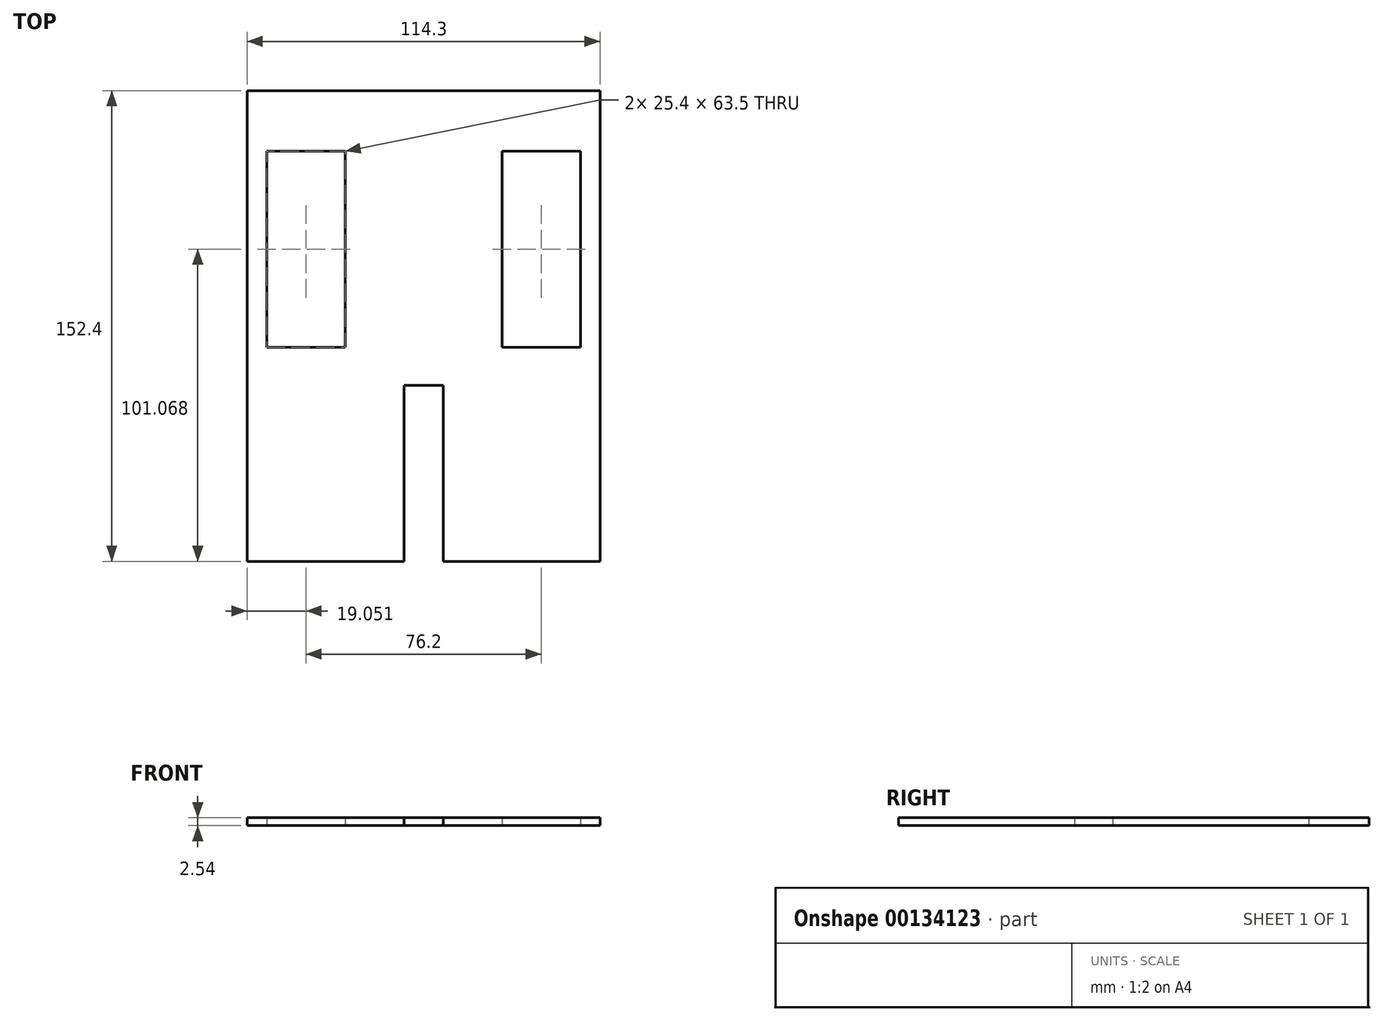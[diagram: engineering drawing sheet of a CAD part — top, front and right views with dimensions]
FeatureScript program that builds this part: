
annotation { "Feature Type Name" : "Feature", "Feature Type Description" : "" }
export const myFeature = defineFeature(function(context is Context, id is Id, definition is map)
    precondition{}
    {
        {
            var Q0;
            Q0=qCreatedBy(makeId("Top.planeOp"),FACE);
            var sketch = newSketch(context, id + "F0", { "sketchPlane" : qUnion([Q0])});
            skLineSegment(sketch, "E0.bottom", {"start": v(-59.3, 79.48) * mm, "end": v(55, 79.48) * mm});
            skLineSegment(sketch, "E0.left", {"start": v(-59.3, 79.48) * mm, "end": v(-59.3, -72.92) * mm});
            skLineSegment(sketch, "E0.right", {"start": v(55, 79.48) * mm, "end": v(55, -72.92) * mm});
            skLineSegment(sketch, "E1.bottom", {"start": v(-59.3, -72.92) * mm, "end": v(-21.2, -72.92) * mm});
            skLineSegment(sketch, "E1.left", {"start": v(-59.3, -72.92) * mm, "end": v(-59.3, -15.91) * mm});
            skLineSegment(sketch, "E2.top", {"start": v(16.9, -72.92) * mm, "end": v(55, -72.92) * mm});
            skLineSegment(sketch, "E2.right", {"start": v(55, -15.91) * mm, "end": v(55, -72.92) * mm});
            skLineSegment(sketch, "E3.bottom", {"start": v(-59.3, -72.92) * mm, "end": v(-52.95, -72.92) * mm});
            skLineSegment(sketch, "E3.left", {"start": v(-59.3, -72.92) * mm, "end": v(-59.3, 50.73) * mm});
            skLineSegment(sketch, "E4.top", {"start": v(-52.95, -72.92) * mm, "end": v(-27.55, -72.92) * mm});
            skPoint(sketch, "E5.oppositeSnap0", {"position": v(-27.55, -11.1) * mm});
            skLineSegment(sketch, "E5.top", {"start": v(-52.95, 59.9) * mm, "end": v(-27.55, 59.9) * mm});
            skLineSegment(sketch, "E5.left", {"start": v(-52.95, 50.73) * mm, "end": v(-52.95, 59.9) * mm});
            skLineSegment(sketch, "E5.right", {"start": v(-27.55, 50.73) * mm, "end": v(-27.55, 59.9) * mm});
            skLineSegment(sketch, "E6.top", {"start": v(-52.95, -3.6) * mm, "end": v(-27.55, -3.6) * mm});
            skLineSegment(sketch, "E6.left", {"start": v(-52.95, 59.9) * mm, "end": v(-52.95, -3.6) * mm});
            skLineSegment(sketch, "E6.right", {"start": v(-27.55, 59.9) * mm, "end": v(-27.55, -3.6) * mm});
            skLineSegment(sketch, "E7.bottom", {"start": v(55, -72.92) * mm, "end": v(48.65, -72.92) * mm});
            skLineSegment(sketch, "E7.left", {"start": v(55, -72.92) * mm, "end": v(55, 59.9) * mm});
            skLineSegment(sketch, "E8.bottom", {"start": v(48.65, 59.9) * mm, "end": v(23.25, 59.9) * mm});
            skLineSegment(sketch, "E8.top", {"start": v(48.65, -3.6) * mm, "end": v(23.25, -3.6) * mm});
            skLineSegment(sketch, "E8.left", {"start": v(48.65, 59.9) * mm, "end": v(48.65, -3.6) * mm});
            skLineSegment(sketch, "E8.right", {"start": v(23.25, 59.9) * mm, "end": v(23.25, -3.6) * mm});
            skLineSegment(sketch, "E9.bottom", {"start": v(-21.2, -72.92) * mm, "end": v(-8.5, -72.92) * mm});
            skLineSegment(sketch, "E10.bottom", {"start": v(-8.5, -15.91) * mm, "end": v(4.2, -15.91) * mm});
            skLineSegment(sketch, "E10.left", {"start": v(-8.5, -15.91) * mm, "end": v(-8.5, -72.92) * mm});
            skLineSegment(sketch, "E10.right", {"start": v(4.2, -15.91) * mm, "end": v(4.2, -72.92) * mm});
            skLineSegment(sketch, "E11", {"start": v(16.9, -72.92) * mm, "end": v(4.2, -72.92) * mm});
            skSolve(sketch);
        }
        {
            var Q0;
            Q0 = qSketchRegion(id + "F0", true);
            extrude(context, id + "F1", {"entities" : qUnion([Q0]), "depth" : 2.54 * mm});
        }
    });
